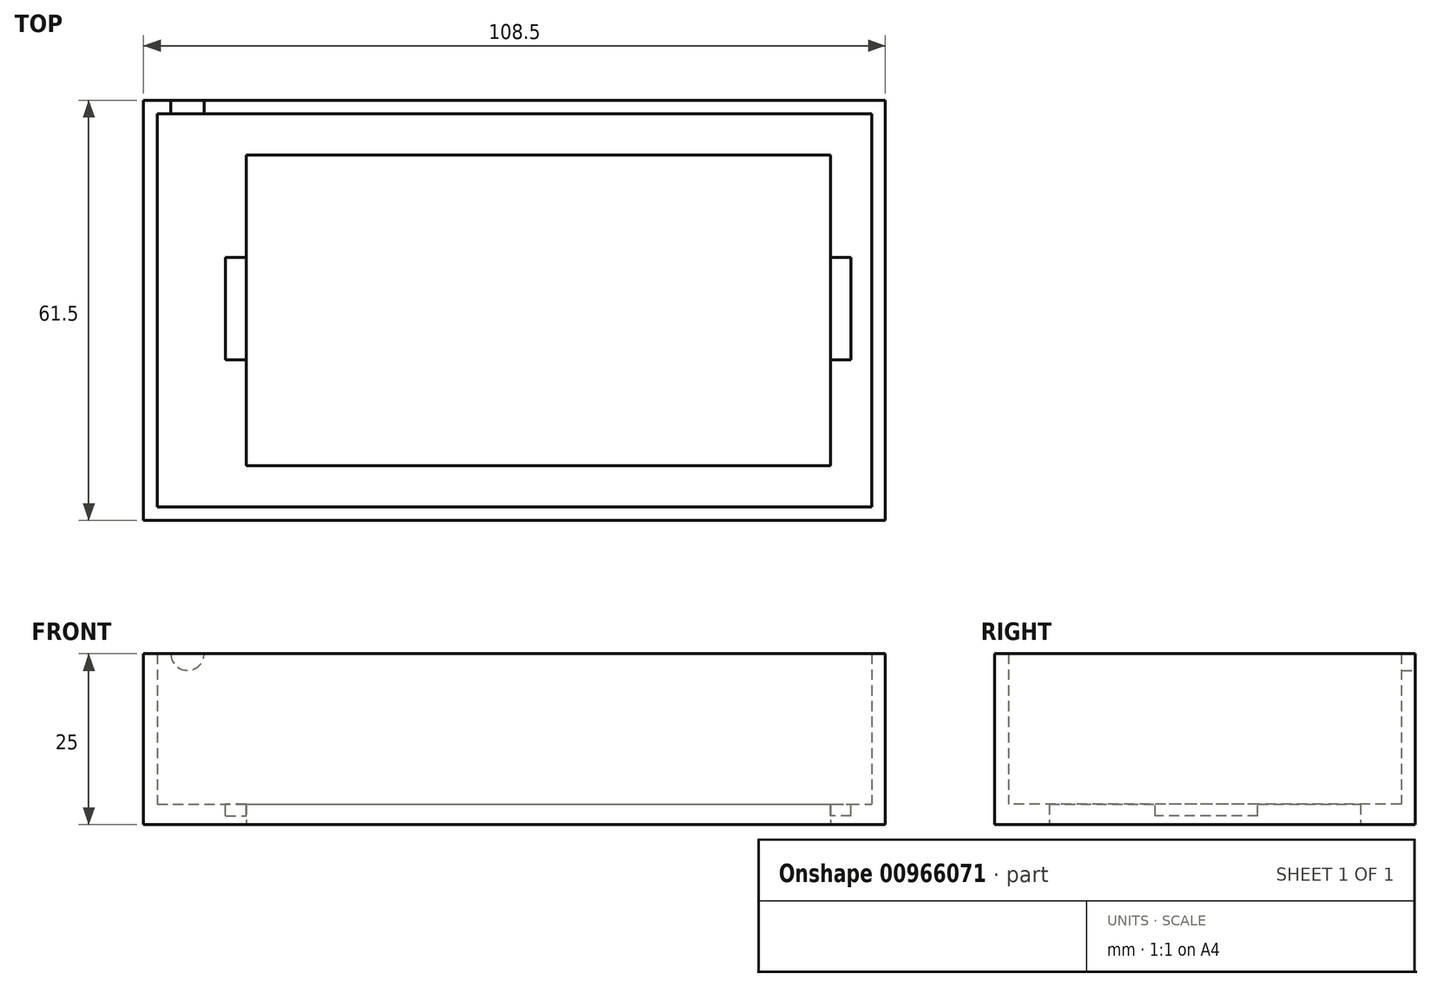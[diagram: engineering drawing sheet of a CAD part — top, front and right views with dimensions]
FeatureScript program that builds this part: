
annotation { "Feature Type Name" : "Feature", "Feature Type Description" : "" }
export const myFeature = defineFeature(function(context is Context, id is Id, definition is map)
    precondition{}
    {
        {
            var Q0;
            Q0=qCreatedBy(makeId("Top.planeOp"),FACE);
            var sketch = newSketch(context, id + "F0", { "sketchPlane" : qUnion([Q0])});
            skLineSegment(sketch, "E0.bottom", {"start": v(0, 0) * mm, "end": v(85.5, 0) * mm});
            skLineSegment(sketch, "E0.top", {"start": v(0, 45.5) * mm, "end": v(85.5, 45.5) * mm});
            skLineSegment(sketch, "E0.left", {"start": v(0, 0) * mm, "end": v(0, 45.5) * mm});
            skLineSegment(sketch, "E0.right", {"start": v(85.5, 0) * mm, "end": v(85.5, 45.5) * mm});
            skLineSegment(sketch, "E1.bottom", {"start": v(93.5, 53.5) * mm, "end": v(-15, 53.5) * mm});
            skLineSegment(sketch, "E1.top", {"start": v(93.5, -8) * mm, "end": v(-15, -8) * mm});
            skLineSegment(sketch, "E1.left", {"start": v(93.5, 53.5) * mm, "end": v(93.5, -8) * mm});
            skLineSegment(sketch, "E1.right", {"start": v(-15, 53.5) * mm, "end": v(-15, -8) * mm});
            skSolve(sketch);
        }
        {
            var Q0;
            Q0=qSketchRegion(id+"F0",true);
            extrude(context, id + "F1", {"entities" : qUnion([Q0]), "depth" : 3 * mm, "offsetDistance" : 25 * mm});
        }
        {
            var Q0;
            Q0=makeQuery(id+"F1.opExtrude","CAP_FACE",FACE,{"disambiguationData":[OSD([sQuery(id+"F0.wireOp",EDGE,"E0.bottom"),sQuery(id+"F0.wireOp",EDGE,"E0.top"),sQuery(id+"F0.wireOp",EDGE,"E0.left"),sQuery(id+"F0.wireOp",EDGE,"E0.right"),sQuery(id+"F0.wireOp",EDGE,"E1.bottom"),sQuery(id+"F0.wireOp",EDGE,"E1.top"),sQuery(id+"F0.wireOp",EDGE,"E1.left"),sQuery(id+"F0.wireOp",EDGE,"E1.right"),sQuery(id+"F0.wireOp",EDGE,"ynSznu6d-FZ8z-CsDZ-gTMR-sA5dCJsNS2Og"),sQuery(id+"F0.wireOp",EDGE,"sdGSAIzi-biUN-54h9-NOsQ-CkFmM2fO8T6S")])],"isStart":false});
            var sketch = newSketch(context, id + "F2", { "sketchPlane" : qUnion([Q0])});
            skLineSegment(sketch, "E2.bottom", {"start": v(0, 30.5) * mm, "end": v(-3, 30.5) * mm});
            skLineSegment(sketch, "E2.top", {"start": v(0, 15.5) * mm, "end": v(-3, 15.5) * mm});
            skLineSegment(sketch, "E2.left", {"start": v(0, 30.5) * mm, "end": v(0, 15.5) * mm});
            skLineSegment(sketch, "E2.right", {"start": v(-3, 30.5) * mm, "end": v(-3, 15.5) * mm});
            skLineSegment(sketch, "E3.bottom", {"start": v(85.5, 30.5) * mm, "end": v(88.5, 30.5) * mm});
            skLineSegment(sketch, "E3.top", {"start": v(85.5, 15.5) * mm, "end": v(88.5, 15.5) * mm});
            skLineSegment(sketch, "E3.left", {"start": v(85.5, 30.5) * mm, "end": v(85.5, 15.5) * mm});
            skLineSegment(sketch, "E3.right", {"start": v(88.5, 30.5) * mm, "end": v(88.5, 15.5) * mm});
            skSolve(sketch);
        }
        {
            var Q0;
            Q0=qSketchRegion(id+"F2",true);
            var Q1;
            Q1=makeQuery(id+"F1.opExtrude","CAP_FACE",FACE,{"disambiguationData":[OSD([sQuery(id+"F0.wireOp",EDGE,"E0.bottom"),sQuery(id+"F0.wireOp",EDGE,"E0.top"),sQuery(id+"F0.wireOp",EDGE,"E0.left"),sQuery(id+"F0.wireOp",EDGE,"E0.right"),sQuery(id+"F0.wireOp",EDGE,"E1.bottom"),sQuery(id+"F0.wireOp",EDGE,"E1.top"),sQuery(id+"F0.wireOp",EDGE,"E1.left"),sQuery(id+"F0.wireOp",EDGE,"E1.right")])],"isStart":true});
            extrude(context, id + "F3", {"entities" : qUnion([Q0]), "operationType" : NewBodyOperationType.REMOVE, "endBound" : BoundingType.UP_TO_SURFACE, "oppositeDirection" : true, "depth" : 3.5 * mm, "endBoundEntityFace" : qUnion([Q1]), "hasOffset" : true, "offsetDistance" : 1.3 * mm});
        }
        {
            var Q0;
            Q0=makeQuery(id+"F1.opExtrude","CAP_FACE",FACE,{"disambiguationData":[OSD([sQuery(id+"F0.wireOp",EDGE,"E0.bottom"),sQuery(id+"F0.wireOp",EDGE,"E0.top"),sQuery(id+"F0.wireOp",EDGE,"E0.left"),sQuery(id+"F0.wireOp",EDGE,"E0.right"),sQuery(id+"F0.wireOp",EDGE,"E1.bottom"),sQuery(id+"F0.wireOp",EDGE,"E1.top"),sQuery(id+"F0.wireOp",EDGE,"E1.left"),sQuery(id+"F0.wireOp",EDGE,"E1.right")])],"isStart":false});
            var sketch = newSketch(context, id + "F4", { "sketchPlane" : qUnion([Q0])});
            skLineSegment(sketch, "E4.bottom", {"start": v(-15, 53.5) * mm, "end": v(93.5, 53.5) * mm});
            skLineSegment(sketch, "E4.top", {"start": v(-15, -8) * mm, "end": v(93.5, -8) * mm});
            skLineSegment(sketch, "E4.left", {"start": v(-15, 53.5) * mm, "end": v(-15, -8) * mm});
            skLineSegment(sketch, "E4.right", {"start": v(93.5, 53.5) * mm, "end": v(93.5, -8) * mm});
            skLineSegment(sketch, "E5.bottom", {"start": v(-13, 51.5) * mm, "end": v(91.5, 51.5) * mm});
            skLineSegment(sketch, "E5.top", {"start": v(-13, -6) * mm, "end": v(91.5, -6) * mm});
            skLineSegment(sketch, "E5.left", {"start": v(-13, 51.5) * mm, "end": v(-13, -6) * mm});
            skLineSegment(sketch, "E5.right", {"start": v(91.5, 51.5) * mm, "end": v(91.5, -6) * mm});
            skSolve(sketch);
        }
        {
            var Q0;
            Q0 = qSketchRegion(id + "F4", true);
            extrude(context, id + "F5", {"entities" : qUnion([Q0]), "operationType" : NewBodyOperationType.ADD, "depth" : 22 * mm, "offsetDistance" : 25 * mm});
        }
        {
            var Q0;
            Q0=makeQuery(id+"F5.boolean.opBoolean","MERGE",FACE,{"derivedFrom":[makeQuery(id+"F1.opExtrude","SWEPT_FACE",FACE,{"disambiguationData":[OSD([sQuery(id+"F0.wireOp",EDGE,"E1.bottom")])]}),makeQuery(id+"F5.opExtrude","SWEPT_FACE",FACE,{"disambiguationData":[OSD([sQuery(id+"F4.wireOp",EDGE,"E4.bottom")])]})]});
            var sketch = newSketch(context, id + "F6", { "sketchPlane" : qUnion([Q0])});
            skArc(sketch, "E6", {"start": v(6.16, 25) * mm, "mid": v(8.58, 22.58) * mm, "end": v(11, 25) * mm});
            skLineSegment(sketch, "E7", {"start": v(6.16, 25) * mm, "end": v(11, 25) * mm});
            skSolve(sketch);
        }
        {
            var Q0;
            Q0 = qSketchRegion(id + "F6", true);
            extrude(context, id + "F7", {"entities" : qUnion([Q0]), "operationType" : NewBodyOperationType.REMOVE, "endBound" : BoundingType.UP_TO_NEXT, "oppositeDirection" : true, "depth" : 25 * mm, "offsetDistance" : 25 * mm});
        }
    });
